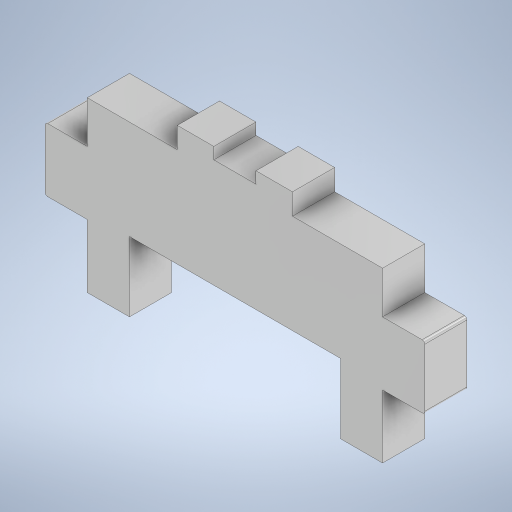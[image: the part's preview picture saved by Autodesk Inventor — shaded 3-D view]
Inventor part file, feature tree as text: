
AUTODESK INVENTOR PART (.ipt)
format: ipt  version: 2024.1 (Build 281209000, 209)  size: 368,128 bytes
history: native  units: mm
features: other x6, extrude x1, sketch x1
ambient origin geometry x8: Origin, YZ Plane, XZ Plane, XY Plane, X Axis, Y Axis, Z Axis, Center Point
bodies: Solide1 (feature_tree)
feature tree (8):
  other  "Blocs"
  extrude  "Extrusion1"  Depth=2.0mm
  other  "Unit"
  other  "Anchor"
  sketch  "Esquisse2"
  other  "Anchor:4"
  other  "Anchor:5"
  other  "Unit:6"
